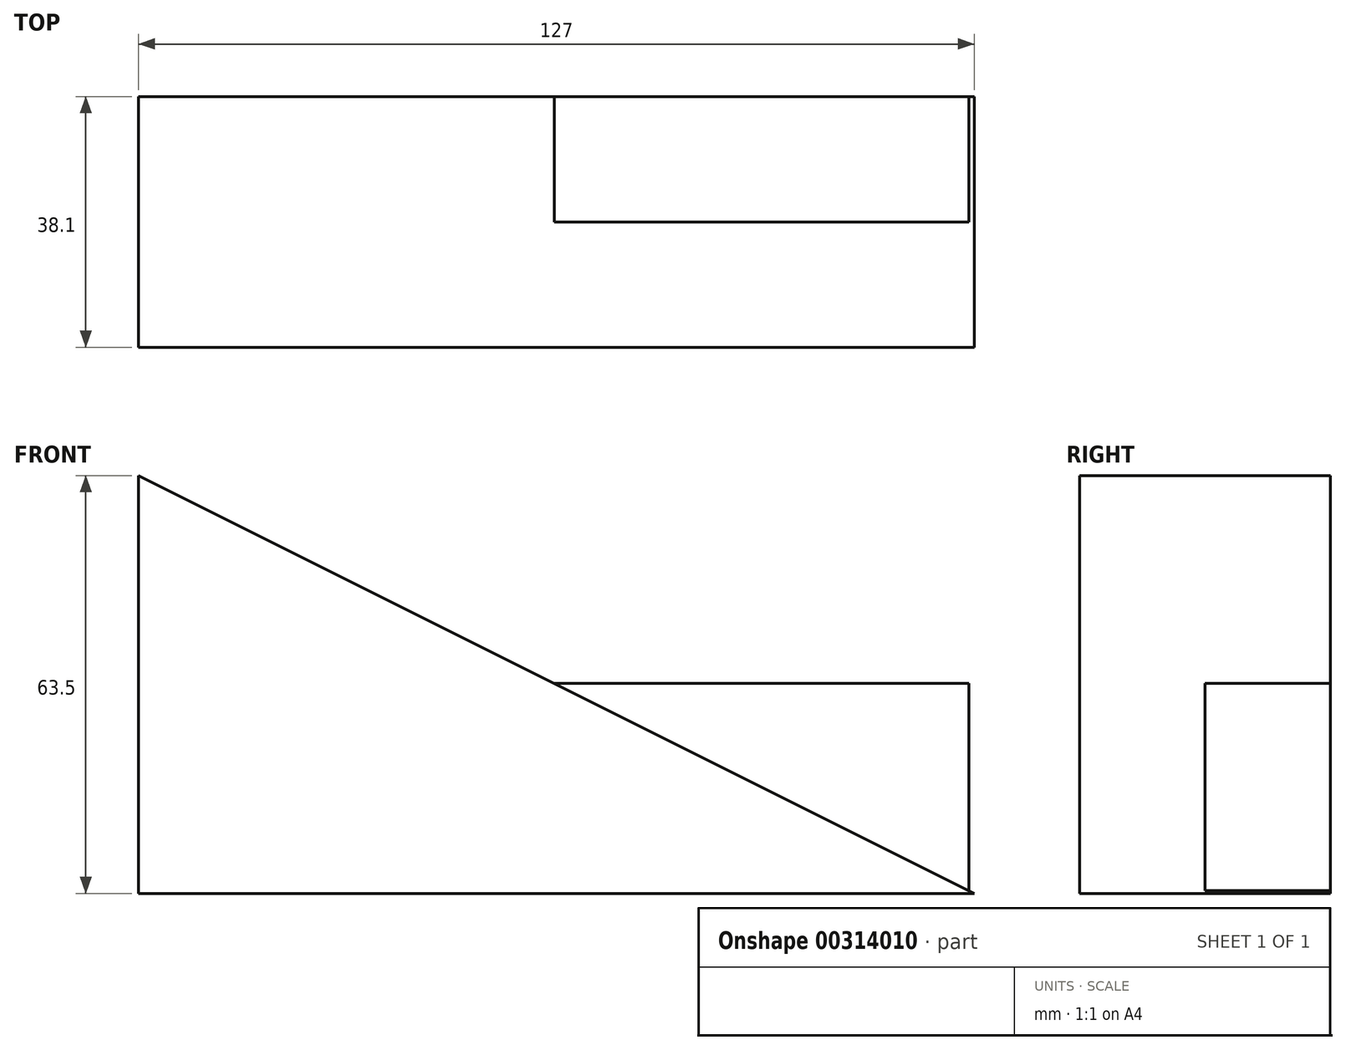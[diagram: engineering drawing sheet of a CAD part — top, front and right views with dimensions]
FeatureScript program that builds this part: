
annotation { "Feature Type Name" : "Feature", "Feature Type Description" : "" }
export const myFeature = defineFeature(function(context is Context, id is Id, definition is map)
    precondition{}
    {
        {
            var Q0;
            Q0=qCreatedBy(makeId("Front.planeOp"),FACE);
            var sketch = newSketch(context, id + "F0", { "sketchPlane" : qUnion([Q0])});
            skLineSegment(sketch, "E0", {"start": v(-65.39, 35.83) * mm, "end": v(-65.39, -27.67) * mm});
            skLineSegment(sketch, "E1", {"start": v(-65.39, -27.67) * mm, "end": v(61.61, -27.67) * mm});
            skLineSegment(sketch, "E2", {"start": v(-65.39, 35.83) * mm, "end": v(61.61, -27.67) * mm});
            skLineSegment(sketch, "E3", {"start": v(61.61, -27.67) * mm, "end": v(61.61, 4.08) * mm});
            skPoint(sketch, "E3.endSnap0", {"position": v(-1.89, 4.08) * mm});
            skLineSegment(sketch, "E4", {"start": v(61.61, 4.08) * mm, "end": v(-1.89, 4.08) * mm});
            skLineSegment(sketch, "E5", {"start": v(-1.89, 4.08) * mm, "end": v(-1.89, -27.67) * mm});
            skLineSegment(sketch, "E6", {"start": v(-1.89, -27.67) * mm, "end": v(61.61, -27.67) * mm});
            skSolve(sketch);
        }
        {
            var Q0;
            {var subQ2=sQuery(id+"F0.wireOp",EDGE,"E5");Q0=makeQuery(id+"F0.imprint","IMPRINT",FACE,{"disambiguationData":[TD([[makeQuery(id+"F0.imprint","IMPRINT",EDGE,{"derivedFrom":subQ2}),1.0]])]});}
            var Q1;
            {var subQ0=sQuery(id+"F0.wireOp",EDGE,"E0");Q1=makeQuery(id+"F0.imprint","IMPRINT",FACE,{"disambiguationData":[TD([[makeQuery(id+"F0.imprint","IMPRINT",EDGE,{"derivedFrom":subQ0}),1.0]])]});}
            extrude(context, id + "F1", {"entities" : qUnion([Q0, Q1]), "depth" : 38.1 * mm});
        }
        {
            var Q0;
            Q0=qCreatedBy(makeId("Front.planeOp"),FACE);
            var sketch = newSketch(context, id + "F2", { "sketchPlane" : qUnion([Q0])});
            skLineSegment(sketch, "E7", {"start": v(60.77, -27.5) * mm, "end": v(60.77, 4.25) * mm});
            skLineSegment(sketch, "E8", {"start": v(60.77, 4.25) * mm, "end": v(-2.73, 4.25) * mm});
            skLineSegment(sketch, "E9", {"start": v(-2.73, 4.25) * mm, "end": v(-2.73, -27.5) * mm});
            skLineSegment(sketch, "E10", {"start": v(-2.73, -27.5) * mm, "end": v(60.77, -27.5) * mm});
            skSolve(sketch);
        }
        {
            var Q0;
            Q0=makeQuery(id+"F2.imprint","IMPRINT",FACE,{"disambiguationData":[TD([[makeQuery(id+"F2.imprint","IMPRINT",EDGE,{"derivedFrom":sQuery(id+"F2.wireOp",EDGE,"E7")}),1.0]])]});
            extrude(context, id + "F3", {"entities" : qUnion([Q0]), "operationType" : NewBodyOperationType.ADD, "depth" : 19.05 * mm});
        }
    });
